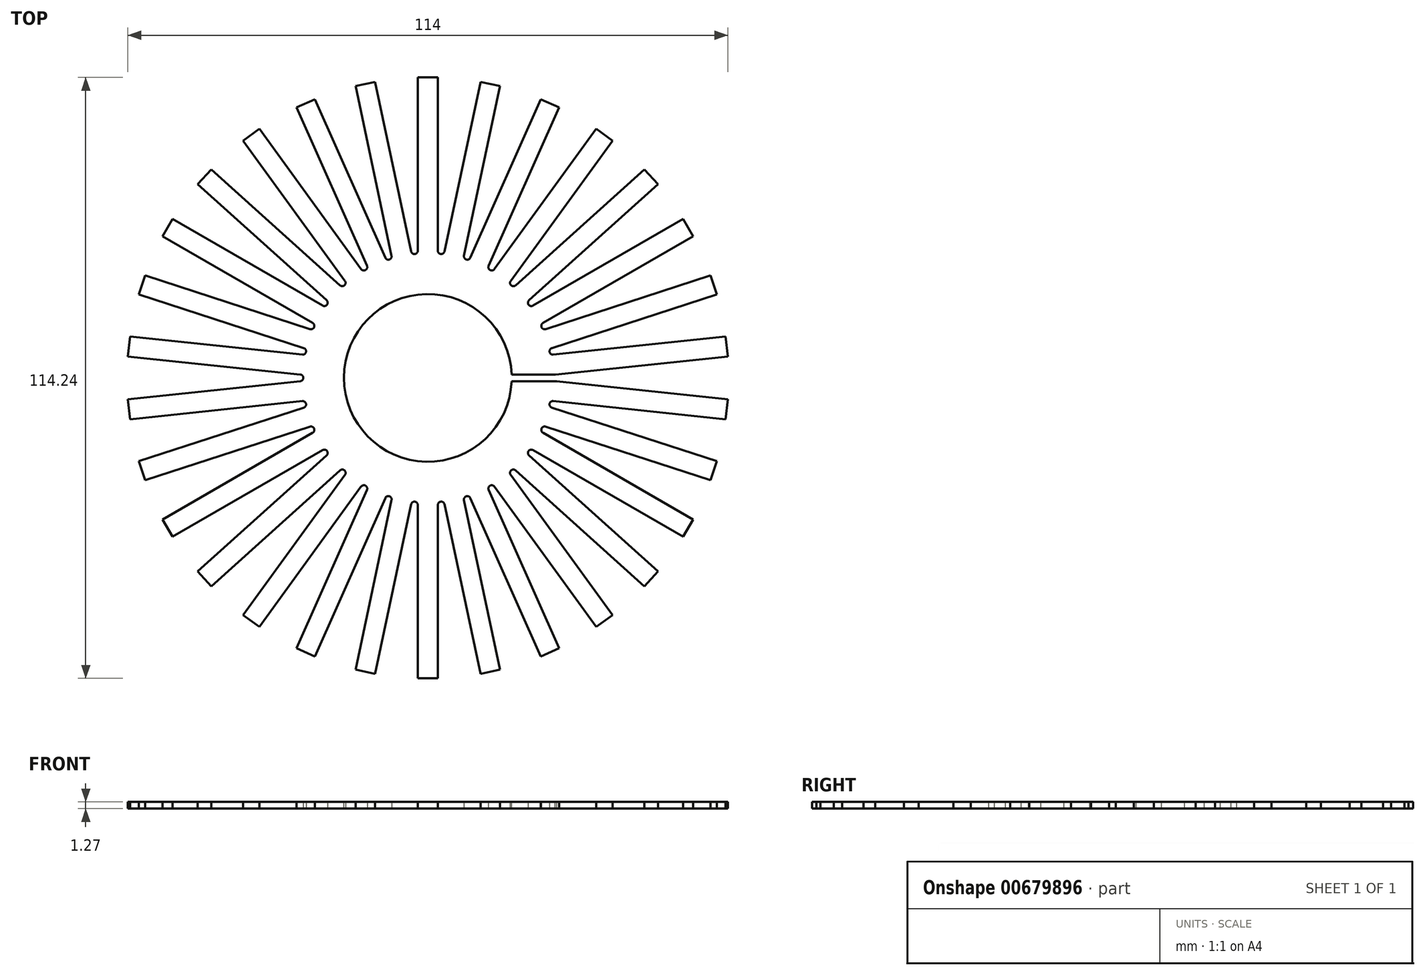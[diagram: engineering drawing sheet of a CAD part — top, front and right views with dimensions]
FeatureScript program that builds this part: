
annotation { "Feature Type Name" : "Feature", "Feature Type Description" : "" }
export const myFeature = defineFeature(function(context is Context, id is Id, definition is map)
    precondition{}
    {
        {
            var Q0;
            Q0=qCreatedBy(makeId("Top.planeOp"),FACE);
            var sketch = newSketch(context, id + "F0", { "sketchPlane" : qUnion([Q0])});
            skCircle(sketch, "E0", {"center": v(0, 0) * mm, "radius": 57.15 * mm, "construction": true});
            skCircle(sketch, "E1", {"center": v(0, 0) * mm, "radius": 13.34 * mm, "construction": true});
            skLineSegment(sketch, "E2.bottom", {"start": v(1.9, 13.2) * mm, "end": v(-1.9, 13.2) * mm});
            skLineSegment(sketch, "E2.top", {"start": v(1.9, 57.12) * mm, "end": v(-1.9, 57.12) * mm});
            skLineSegment(sketch, "E2.left", {"start": v(1.9, 13.2) * mm, "end": v(1.9, 57.12) * mm});
            skLineSegment(sketch, "E2.right", {"start": v(-1.9, 13.2) * mm, "end": v(-1.9, 57.12) * mm});
            skCircle(sketch, "E3.1.1", {"center": v(0, 0) * mm, "radius": 13.33 * mm, "construction": true});
            skLineSegment(sketch, "E3.1.2", {"start": v(-0.88, 13.3) * mm, "end": v(-10.01, 56.27) * mm});
            skLineSegment(sketch, "E3.1.3", {"start": v(-4.6, 12.51) * mm, "end": v(-13.74, 55.47) * mm});
            skLineSegment(sketch, "E3.1.4", {"start": v(-0.88, 13.3) * mm, "end": v(-4.6, 12.51) * mm});
            skLineSegment(sketch, "E3.1.5", {"start": v(-10.01, 56.27) * mm, "end": v(-13.74, 55.47) * mm});
            skLineSegment(sketch, "E3.2.2", {"start": v(-3.63, 12.83) * mm, "end": v(-21.5, 52.95) * mm});
            skLineSegment(sketch, "E3.2.3", {"start": v(-7.1, 11.28) * mm, "end": v(-24.97, 51.4) * mm});
            skLineSegment(sketch, "E3.2.4", {"start": v(-3.63, 12.83) * mm, "end": v(-7.1, 11.28) * mm});
            skLineSegment(sketch, "E3.2.5", {"start": v(-21.5, 52.95) * mm, "end": v(-24.97, 51.4) * mm});
            skLineSegment(sketch, "E3.3.2", {"start": v(-6.22, 11.8) * mm, "end": v(-32.03, 47.33) * mm});
            skLineSegment(sketch, "E3.3.3", {"start": v(-9.3, 9.56) * mm, "end": v(-35.11, 45.09) * mm});
            skLineSegment(sketch, "E3.3.4", {"start": v(-6.22, 11.8) * mm, "end": v(-9.3, 9.56) * mm});
            skLineSegment(sketch, "E3.3.5", {"start": v(-32.03, 47.33) * mm, "end": v(-35.11, 45.09) * mm});
            skCircle(sketch, "E3.4.1", {"center": v(0, 0) * mm, "radius": 13.33 * mm, "construction": true});
            skLineSegment(sketch, "E3.4.2", {"start": v(-8.53, 10.25) * mm, "end": v(-41.17, 39.64) * mm});
            skLineSegment(sketch, "E3.4.3", {"start": v(-11.08, 7.42) * mm, "end": v(-43.72, 36.8) * mm});
            skLineSegment(sketch, "E3.4.4", {"start": v(-8.53, 10.25) * mm, "end": v(-11.08, 7.42) * mm});
            skLineSegment(sketch, "E3.4.5", {"start": v(-41.17, 39.64) * mm, "end": v(-43.72, 36.8) * mm});
            skLineSegment(sketch, "E3.5.2", {"start": v(-10.48, 8.25) * mm, "end": v(-48.51, 30.2) * mm});
            skLineSegment(sketch, "E3.5.3", {"start": v(-12.38, 4.95) * mm, "end": v(-50.42, 26.9) * mm});
            skLineSegment(sketch, "E3.5.4", {"start": v(-10.48, 8.25) * mm, "end": v(-12.38, 4.95) * mm});
            skLineSegment(sketch, "E3.5.5", {"start": v(-48.51, 30.2) * mm, "end": v(-50.42, 26.9) * mm});
            skLineSegment(sketch, "E3.6.2", {"start": v(-11.96, 5.9) * mm, "end": v(-53.73, 19.46) * mm});
            skLineSegment(sketch, "E3.6.3", {"start": v(-13.14, 2.27) * mm, "end": v(-54.91, 15.84) * mm});
            skLineSegment(sketch, "E3.6.4", {"start": v(-11.96, 5.9) * mm, "end": v(-13.14, 2.27) * mm});
            skLineSegment(sketch, "E3.6.5", {"start": v(-53.73, 19.46) * mm, "end": v(-54.91, 15.84) * mm});
            skCircle(sketch, "E3.7.1", {"center": v(0, 0) * mm, "radius": 13.33 * mm, "construction": true});
            skLineSegment(sketch, "E3.7.2", {"start": v(-12.93, 3.27) * mm, "end": v(-56.6, 7.87) * mm});
            skLineSegment(sketch, "E3.7.3", {"start": v(-13.33, -0.51) * mm, "end": v(-57, 4.08) * mm});
            skLineSegment(sketch, "E3.7.4", {"start": v(-12.93, 3.27) * mm, "end": v(-13.33, -0.51) * mm});
            skLineSegment(sketch, "E3.7.5", {"start": v(-56.6, 7.87) * mm, "end": v(-57, 4.08) * mm});
            skLineSegment(sketch, "E3.8.2", {"start": v(-13.33, 0.51) * mm, "end": v(-57, -4.08) * mm});
            skLineSegment(sketch, "E3.8.3", {"start": v(-12.93, -3.27) * mm, "end": v(-56.6, -7.87) * mm});
            skLineSegment(sketch, "E3.8.4", {"start": v(-13.33, 0.51) * mm, "end": v(-12.93, -3.27) * mm});
            skLineSegment(sketch, "E3.8.5", {"start": v(-57, -4.08) * mm, "end": v(-56.6, -7.87) * mm});
            skLineSegment(sketch, "E3.9.2", {"start": v(-13.14, -2.27) * mm, "end": v(-54.91, -15.84) * mm});
            skLineSegment(sketch, "E3.9.3", {"start": v(-11.96, -5.9) * mm, "end": v(-53.73, -19.46) * mm});
            skLineSegment(sketch, "E3.9.4", {"start": v(-13.14, -2.27) * mm, "end": v(-11.96, -5.9) * mm});
            skLineSegment(sketch, "E3.9.5", {"start": v(-54.91, -15.84) * mm, "end": v(-53.73, -19.46) * mm});
            skLineSegment(sketch, "E3.10.2", {"start": v(-12.38, -4.95) * mm, "end": v(-50.42, -26.9) * mm});
            skLineSegment(sketch, "E3.10.3", {"start": v(-10.48, -8.25) * mm, "end": v(-48.51, -30.2) * mm});
            skLineSegment(sketch, "E3.10.4", {"start": v(-12.38, -4.95) * mm, "end": v(-10.48, -8.25) * mm});
            skLineSegment(sketch, "E3.10.5", {"start": v(-50.42, -26.9) * mm, "end": v(-48.51, -30.2) * mm});
            skLineSegment(sketch, "E3.11.2", {"start": v(-11.08, -7.42) * mm, "end": v(-43.72, -36.8) * mm});
            skLineSegment(sketch, "E3.11.3", {"start": v(-8.53, -10.25) * mm, "end": v(-41.17, -39.64) * mm});
            skLineSegment(sketch, "E3.11.4", {"start": v(-11.08, -7.42) * mm, "end": v(-8.53, -10.25) * mm});
            skLineSegment(sketch, "E3.11.5", {"start": v(-43.72, -36.8) * mm, "end": v(-41.17, -39.64) * mm});
            skLineSegment(sketch, "E3.12.2", {"start": v(-9.3, -9.56) * mm, "end": v(-35.11, -45.09) * mm});
            skLineSegment(sketch, "E3.12.3", {"start": v(-6.22, -11.8) * mm, "end": v(-32.03, -47.33) * mm});
            skLineSegment(sketch, "E3.12.4", {"start": v(-9.3, -9.56) * mm, "end": v(-6.22, -11.8) * mm});
            skLineSegment(sketch, "E3.12.5", {"start": v(-35.11, -45.09) * mm, "end": v(-32.03, -47.33) * mm});
            skLineSegment(sketch, "E3.13.2", {"start": v(-7.1, -11.28) * mm, "end": v(-24.97, -51.4) * mm});
            skLineSegment(sketch, "E3.13.3", {"start": v(-3.63, -12.83) * mm, "end": v(-21.5, -52.95) * mm});
            skLineSegment(sketch, "E3.13.4", {"start": v(-7.1, -11.28) * mm, "end": v(-3.63, -12.83) * mm});
            skLineSegment(sketch, "E3.13.5", {"start": v(-24.97, -51.4) * mm, "end": v(-21.5, -52.95) * mm});
            skCircle(sketch, "E3.14.1", {"center": v(0, 0) * mm, "radius": 13.33 * mm, "construction": true});
            skLineSegment(sketch, "E3.14.2", {"start": v(-4.6, -12.51) * mm, "end": v(-13.74, -55.47) * mm});
            skLineSegment(sketch, "E3.14.3", {"start": v(-0.88, -13.3) * mm, "end": v(-10.01, -56.27) * mm});
            skLineSegment(sketch, "E3.14.4", {"start": v(-4.6, -12.51) * mm, "end": v(-0.88, -13.3) * mm});
            skLineSegment(sketch, "E3.14.5", {"start": v(-13.74, -55.47) * mm, "end": v(-10.01, -56.27) * mm});
            skLineSegment(sketch, "E3.15.2", {"start": v(-1.9, -13.2) * mm, "end": v(-1.9, -57.12) * mm});
            skLineSegment(sketch, "E3.15.3", {"start": v(1.9, -13.2) * mm, "end": v(1.9, -57.12) * mm});
            skLineSegment(sketch, "E3.15.4", {"start": v(-1.9, -13.2) * mm, "end": v(1.9, -13.2) * mm});
            skLineSegment(sketch, "E3.15.5", {"start": v(-1.9, -57.12) * mm, "end": v(1.9, -57.12) * mm});
            skCircle(sketch, "E3.16.1", {"center": v(0, 0) * mm, "radius": 13.33 * mm, "construction": true});
            skLineSegment(sketch, "E3.16.2", {"start": v(0.88, -13.3) * mm, "end": v(10.01, -56.27) * mm});
            skLineSegment(sketch, "E3.16.3", {"start": v(4.6, -12.51) * mm, "end": v(13.74, -55.47) * mm});
            skLineSegment(sketch, "E3.16.4", {"start": v(0.88, -13.3) * mm, "end": v(4.6, -12.51) * mm});
            skLineSegment(sketch, "E3.16.5", {"start": v(10.01, -56.27) * mm, "end": v(13.74, -55.47) * mm});
            skLineSegment(sketch, "E3.17.2", {"start": v(3.63, -12.83) * mm, "end": v(21.5, -52.95) * mm});
            skLineSegment(sketch, "E3.17.3", {"start": v(7.1, -11.28) * mm, "end": v(24.97, -51.4) * mm});
            skLineSegment(sketch, "E3.17.4", {"start": v(3.63, -12.83) * mm, "end": v(7.1, -11.28) * mm});
            skLineSegment(sketch, "E3.17.5", {"start": v(21.5, -52.95) * mm, "end": v(24.97, -51.4) * mm});
            skLineSegment(sketch, "E3.18.2", {"start": v(6.22, -11.8) * mm, "end": v(32.03, -47.33) * mm});
            skLineSegment(sketch, "E3.18.3", {"start": v(9.3, -9.56) * mm, "end": v(35.11, -45.09) * mm});
            skLineSegment(sketch, "E3.18.4", {"start": v(6.22, -11.8) * mm, "end": v(9.3, -9.56) * mm});
            skLineSegment(sketch, "E3.18.5", {"start": v(32.03, -47.33) * mm, "end": v(35.11, -45.09) * mm});
            skCircle(sketch, "E3.19.1", {"center": v(0, 0) * mm, "radius": 13.33 * mm, "construction": true});
            skLineSegment(sketch, "E3.19.2", {"start": v(8.53, -10.25) * mm, "end": v(41.17, -39.64) * mm});
            skLineSegment(sketch, "E3.19.3", {"start": v(11.08, -7.42) * mm, "end": v(43.72, -36.8) * mm});
            skLineSegment(sketch, "E3.19.4", {"start": v(8.53, -10.25) * mm, "end": v(11.08, -7.42) * mm});
            skLineSegment(sketch, "E3.19.5", {"start": v(41.17, -39.64) * mm, "end": v(43.72, -36.8) * mm});
            skLineSegment(sketch, "E4.4.20.0", {"start": v(10.48, -8.25) * mm, "end": v(48.51, -30.2) * mm});
            skLineSegment(sketch, "E4.7.20.0", {"start": v(12.38, -4.95) * mm, "end": v(50.42, -26.9) * mm});
            skLineSegment(sketch, "E4.10.20.0", {"start": v(10.48, -8.25) * mm, "end": v(12.38, -4.95) * mm});
            skLineSegment(sketch, "E4.13.20.0", {"start": v(48.51, -30.2) * mm, "end": v(50.42, -26.9) * mm});
            skLineSegment(sketch, "E4.4.21.0", {"start": v(11.96, -5.9) * mm, "end": v(53.73, -19.46) * mm});
            skLineSegment(sketch, "E4.7.21.0", {"start": v(13.14, -2.27) * mm, "end": v(54.91, -15.84) * mm});
            skLineSegment(sketch, "E4.10.21.0", {"start": v(11.96, -5.9) * mm, "end": v(13.14, -2.27) * mm});
            skLineSegment(sketch, "E4.13.21.0", {"start": v(53.73, -19.46) * mm, "end": v(54.91, -15.84) * mm});
            skLineSegment(sketch, "E4.4.22.0", {"start": v(12.93, -3.27) * mm, "end": v(56.6, -7.87) * mm});
            skLineSegment(sketch, "E4.7.22.0", {"start": v(13.33, 0.51) * mm, "end": v(57, -4.08) * mm});
            skLineSegment(sketch, "E4.10.22.0", {"start": v(12.93, -3.27) * mm, "end": v(13.33, 0.51) * mm});
            skLineSegment(sketch, "E4.13.22.0", {"start": v(56.6, -7.87) * mm, "end": v(57, -4.08) * mm});
            skLineSegment(sketch, "E4.4.23.0", {"start": v(13.33, -0.51) * mm, "end": v(57, 4.08) * mm});
            skLineSegment(sketch, "E4.7.23.0", {"start": v(12.93, 3.27) * mm, "end": v(56.6, 7.87) * mm});
            skLineSegment(sketch, "E4.10.23.0", {"start": v(13.33, -0.51) * mm, "end": v(12.93, 3.27) * mm});
            skLineSegment(sketch, "E4.13.23.0", {"start": v(57, 4.08) * mm, "end": v(56.6, 7.87) * mm});
            skLineSegment(sketch, "E4.4.24.0", {"start": v(13.14, 2.27) * mm, "end": v(54.91, 15.84) * mm});
            skLineSegment(sketch, "E4.7.24.0", {"start": v(11.96, 5.9) * mm, "end": v(53.73, 19.46) * mm});
            skLineSegment(sketch, "E4.10.24.0", {"start": v(13.14, 2.27) * mm, "end": v(11.96, 5.9) * mm});
            skLineSegment(sketch, "E4.13.24.0", {"start": v(54.91, 15.84) * mm, "end": v(53.73, 19.46) * mm});
            skLineSegment(sketch, "E5.4.25.0", {"start": v(12.38, 4.95) * mm, "end": v(50.42, 26.9) * mm});
            skLineSegment(sketch, "E5.7.25.0", {"start": v(10.48, 8.25) * mm, "end": v(48.51, 30.2) * mm});
            skLineSegment(sketch, "E5.10.25.0", {"start": v(12.38, 4.95) * mm, "end": v(10.48, 8.25) * mm});
            skLineSegment(sketch, "E5.13.25.0", {"start": v(50.42, 26.9) * mm, "end": v(48.51, 30.2) * mm});
            skLineSegment(sketch, "E5.4.26.0", {"start": v(11.08, 7.42) * mm, "end": v(43.72, 36.8) * mm});
            skLineSegment(sketch, "E5.7.26.0", {"start": v(8.53, 10.25) * mm, "end": v(41.17, 39.64) * mm});
            skLineSegment(sketch, "E5.10.26.0", {"start": v(11.08, 7.42) * mm, "end": v(8.53, 10.25) * mm});
            skLineSegment(sketch, "E5.13.26.0", {"start": v(43.72, 36.8) * mm, "end": v(41.17, 39.64) * mm});
            skLineSegment(sketch, "E5.4.27.0", {"start": v(9.3, 9.56) * mm, "end": v(35.11, 45.09) * mm});
            skLineSegment(sketch, "E5.7.27.0", {"start": v(6.22, 11.8) * mm, "end": v(32.03, 47.33) * mm});
            skLineSegment(sketch, "E5.10.27.0", {"start": v(9.3, 9.56) * mm, "end": v(6.22, 11.8) * mm});
            skLineSegment(sketch, "E5.13.27.0", {"start": v(35.11, 45.09) * mm, "end": v(32.03, 47.33) * mm});
            skLineSegment(sketch, "E5.4.28.0", {"start": v(7.1, 11.28) * mm, "end": v(24.97, 51.4) * mm});
            skLineSegment(sketch, "E5.7.28.0", {"start": v(3.63, 12.83) * mm, "end": v(21.5, 52.95) * mm});
            skLineSegment(sketch, "E5.10.28.0", {"start": v(7.1, 11.28) * mm, "end": v(3.63, 12.83) * mm});
            skLineSegment(sketch, "E5.13.28.0", {"start": v(24.97, 51.4) * mm, "end": v(21.5, 52.95) * mm});
            skLineSegment(sketch, "E5.4.29.0", {"start": v(4.6, 12.51) * mm, "end": v(13.74, 55.47) * mm});
            skLineSegment(sketch, "E5.7.29.0", {"start": v(0.88, 13.3) * mm, "end": v(10.01, 56.27) * mm});
            skLineSegment(sketch, "E5.10.29.0", {"start": v(4.6, 12.51) * mm, "end": v(0.88, 13.3) * mm});
            skLineSegment(sketch, "E5.13.29.0", {"start": v(13.74, 55.47) * mm, "end": v(10.01, 56.27) * mm});
            skSolve(sketch);
        }
        {
            var Q0;
            Q0 = qSketchRegion(id + "F0", true);
            extrude(context, id + "F1", {"entities" : qUnion([Q0]), "depth" : 1.27 * mm, "offsetDistance" : 25.4 * mm});
        }
        {
            var Q0;
            Q0=makeQuery(id+"F1.opExtrude","CAP_FACE",FACE,{"disambiguationData":[OSD([sQuery(id+"F0.wireOp",EDGE,"E2.bottom"),sQuery(id+"F0.wireOp",EDGE,"E2.top"),sQuery(id+"F0.wireOp",EDGE,"E2.left"),sQuery(id+"F0.wireOp",EDGE,"E2.right"),sQuery(id+"F0.wireOp",EDGE,"E3.1.2"),sQuery(id+"F0.wireOp",EDGE,"E3.1.3"),sQuery(id+"F0.wireOp",EDGE,"E3.1.4"),sQuery(id+"F0.wireOp",EDGE,"E3.1.5"),sQuery(id+"F0.wireOp",EDGE,"E3.2.2"),sQuery(id+"F0.wireOp",EDGE,"E3.2.3"),sQuery(id+"F0.wireOp",EDGE,"E3.2.4"),sQuery(id+"F0.wireOp",EDGE,"E3.2.5"),sQuery(id+"F0.wireOp",EDGE,"E3.3.2"),sQuery(id+"F0.wireOp",EDGE,"E3.3.3"),sQuery(id+"F0.wireOp",EDGE,"E3.3.4"),sQuery(id+"F0.wireOp",EDGE,"E3.3.5"),sQuery(id+"F0.wireOp",EDGE,"E3.4.2"),sQuery(id+"F0.wireOp",EDGE,"E3.4.3"),sQuery(id+"F0.wireOp",EDGE,"E3.4.4"),sQuery(id+"F0.wireOp",EDGE,"E3.4.5"),sQuery(id+"F0.wireOp",EDGE,"E3.5.2"),sQuery(id+"F0.wireOp",EDGE,"E3.5.3"),sQuery(id+"F0.wireOp",EDGE,"E3.5.4"),sQuery(id+"F0.wireOp",EDGE,"E3.5.5"),sQuery(id+"F0.wireOp",EDGE,"E3.6.2"),sQuery(id+"F0.wireOp",EDGE,"E3.6.3"),sQuery(id+"F0.wireOp",EDGE,"E3.6.4"),sQuery(id+"F0.wireOp",EDGE,"E3.6.5"),sQuery(id+"F0.wireOp",EDGE,"E3.7.2"),sQuery(id+"F0.wireOp",EDGE,"E3.7.3"),sQuery(id+"F0.wireOp",EDGE,"E3.7.4"),sQuery(id+"F0.wireOp",EDGE,"E3.7.5"),sQuery(id+"F0.wireOp",EDGE,"E3.8.2"),sQuery(id+"F0.wireOp",EDGE,"E3.8.3"),sQuery(id+"F0.wireOp",EDGE,"E3.8.4"),sQuery(id+"F0.wireOp",EDGE,"E3.8.5"),sQuery(id+"F0.wireOp",EDGE,"E3.9.2"),sQuery(id+"F0.wireOp",EDGE,"E3.9.3"),sQuery(id+"F0.wireOp",EDGE,"E3.9.4"),sQuery(id+"F0.wireOp",EDGE,"E3.9.5"),sQuery(id+"F0.wireOp",EDGE,"E3.10.2"),sQuery(id+"F0.wireOp",EDGE,"E3.10.3"),sQuery(id+"F0.wireOp",EDGE,"E3.10.4"),sQuery(id+"F0.wireOp",EDGE,"E3.10.5"),sQuery(id+"F0.wireOp",EDGE,"E3.11.2"),sQuery(id+"F0.wireOp",EDGE,"E3.11.3"),sQuery(id+"F0.wireOp",EDGE,"E3.11.4"),sQuery(id+"F0.wireOp",EDGE,"E3.11.5"),sQuery(id+"F0.wireOp",EDGE,"E3.12.2"),sQuery(id+"F0.wireOp",EDGE,"E3.12.3"),sQuery(id+"F0.wireOp",EDGE,"E3.12.4"),sQuery(id+"F0.wireOp",EDGE,"E3.12.5"),sQuery(id+"F0.wireOp",EDGE,"E3.13.2"),sQuery(id+"F0.wireOp",EDGE,"E3.13.3"),sQuery(id+"F0.wireOp",EDGE,"E3.13.4"),sQuery(id+"F0.wireOp",EDGE,"E3.13.5"),sQuery(id+"F0.wireOp",EDGE,"E3.14.2"),sQuery(id+"F0.wireOp",EDGE,"E3.14.3"),sQuery(id+"F0.wireOp",EDGE,"E3.14.4"),sQuery(id+"F0.wireOp",EDGE,"E3.14.5"),sQuery(id+"F0.wireOp",EDGE,"E3.15.2"),sQuery(id+"F0.wireOp",EDGE,"E3.15.3"),sQuery(id+"F0.wireOp",EDGE,"E3.15.4"),sQuery(id+"F0.wireOp",EDGE,"E3.15.5"),sQuery(id+"F0.wireOp",EDGE,"E3.16.2"),sQuery(id+"F0.wireOp",EDGE,"E3.16.3"),sQuery(id+"F0.wireOp",EDGE,"E3.16.4"),sQuery(id+"F0.wireOp",EDGE,"E3.16.5"),sQuery(id+"F0.wireOp",EDGE,"E3.17.2"),sQuery(id+"F0.wireOp",EDGE,"E3.17.3"),sQuery(id+"F0.wireOp",EDGE,"E3.17.4"),sQuery(id+"F0.wireOp",EDGE,"E3.17.5"),sQuery(id+"F0.wireOp",EDGE,"E3.18.2"),sQuery(id+"F0.wireOp",EDGE,"E3.18.3"),sQuery(id+"F0.wireOp",EDGE,"E3.18.4"),sQuery(id+"F0.wireOp",EDGE,"E3.18.5"),sQuery(id+"F0.wireOp",EDGE,"E3.19.2"),sQuery(id+"F0.wireOp",EDGE,"E3.19.3"),sQuery(id+"F0.wireOp",EDGE,"E3.19.4"),sQuery(id+"F0.wireOp",EDGE,"E3.19.5"),sQuery(id+"F0.wireOp",EDGE,"E4.4.20.0"),sQuery(id+"F0.wireOp",EDGE,"E4.7.20.0"),sQuery(id+"F0.wireOp",EDGE,"E4.10.20.0"),sQuery(id+"F0.wireOp",EDGE,"E4.13.20.0"),sQuery(id+"F0.wireOp",EDGE,"E4.4.21.0"),sQuery(id+"F0.wireOp",EDGE,"E4.7.21.0"),sQuery(id+"F0.wireOp",EDGE,"E4.10.21.0"),sQuery(id+"F0.wireOp",EDGE,"E4.13.21.0"),sQuery(id+"F0.wireOp",EDGE,"E4.4.22.0"),sQuery(id+"F0.wireOp",EDGE,"E4.7.22.0"),sQuery(id+"F0.wireOp",EDGE,"E4.10.22.0"),sQuery(id+"F0.wireOp",EDGE,"E4.13.22.0"),sQuery(id+"F0.wireOp",EDGE,"E4.4.23.0"),sQuery(id+"F0.wireOp",EDGE,"E4.7.23.0"),sQuery(id+"F0.wireOp",EDGE,"E4.10.23.0"),sQuery(id+"F0.wireOp",EDGE,"E4.13.23.0"),sQuery(id+"F0.wireOp",EDGE,"E4.4.24.0"),sQuery(id+"F0.wireOp",EDGE,"E4.7.24.0"),sQuery(id+"F0.wireOp",EDGE,"E4.10.24.0"),sQuery(id+"F0.wireOp",EDGE,"E4.13.24.0"),sQuery(id+"F0.wireOp",EDGE,"E5.4.25.0"),sQuery(id+"F0.wireOp",EDGE,"E5.7.25.0"),sQuery(id+"F0.wireOp",EDGE,"E5.10.25.0"),sQuery(id+"F0.wireOp",EDGE,"E5.13.25.0"),sQuery(id+"F0.wireOp",EDGE,"E5.4.26.0"),sQuery(id+"F0.wireOp",EDGE,"E5.7.26.0"),sQuery(id+"F0.wireOp",EDGE,"E5.10.26.0"),sQuery(id+"F0.wireOp",EDGE,"E5.13.26.0"),sQuery(id+"F0.wireOp",EDGE,"E5.4.27.0"),sQuery(id+"F0.wireOp",EDGE,"E5.7.27.0"),sQuery(id+"F0.wireOp",EDGE,"E5.10.27.0"),sQuery(id+"F0.wireOp",EDGE,"E5.13.27.0"),sQuery(id+"F0.wireOp",EDGE,"E5.4.28.0"),sQuery(id+"F0.wireOp",EDGE,"E5.7.28.0"),sQuery(id+"F0.wireOp",EDGE,"E5.10.28.0"),sQuery(id+"F0.wireOp",EDGE,"E5.13.28.0"),sQuery(id+"F0.wireOp",EDGE,"E5.4.29.0"),sQuery(id+"F0.wireOp",EDGE,"E5.7.29.0"),sQuery(id+"F0.wireOp",EDGE,"E5.10.29.0"),sQuery(id+"F0.wireOp",EDGE,"E5.13.29.0")])],"isStart":false});
            var sketch = newSketch(context, id + "F2", { "sketchPlane" : qUnion([Q0])});
            skCircle(sketch, "E6", {"center": v(0, 0) * mm, "radius": 15.94 * mm});
            skSolve(sketch);
        }
        {
            var Q0;
            Q0 = qSketchRegion(id + "F2", true);
            extrude(context, id + "F3", {"entities" : qUnion([Q0]), "operationType" : NewBodyOperationType.REMOVE, "oppositeDirection" : true, "depth" : 25.4 * mm, "offsetDistance" : 25.4 * mm});
        }
        {
            var Q0;
            Q0=makeQuery(id+"F1.opExtrude","SWEPT_EDGE",EDGE,{"disambiguationData":[OSD([sQuery(id+"F0.wireOp",EDGE,"E3.3.3"),sQuery(id+"F0.wireOp",EDGE,"E3.4.2")])]});
            fillet(context, id + "F4", {"entities" : qUnion([Q0]), "radius" : 0.64 * mm, "tangentPropagation" : true, "allowEdgeOverflow" : false});
        }
        {
            var Q0;
            Q0=makeQuery(id+"F1.opExtrude","SWEPT_EDGE",EDGE,{"disambiguationData":[OSD([sQuery(id+"F0.wireOp",EDGE,"E3.2.3"),sQuery(id+"F0.wireOp",EDGE,"E3.3.2")])]});
            var Q1;
            Q1=makeQuery(id+"F1.opExtrude","SWEPT_EDGE",EDGE,{"disambiguationData":[OSD([sQuery(id+"F0.wireOp",EDGE,"E2.right"),sQuery(id+"F0.wireOp",EDGE,"E3.1.2")])]});
            var Q2;
            Q2=makeQuery(id+"F1.opExtrude","SWEPT_EDGE",EDGE,{"disambiguationData":[OSD([sQuery(id+"F0.wireOp",EDGE,"E2.left"),sQuery(id+"F0.wireOp",EDGE,"E5.7.29.0")])]});
            var Q3;
            Q3=makeQuery(id+"F1.opExtrude","SWEPT_EDGE",EDGE,{"disambiguationData":[OSD([sQuery(id+"F0.wireOp",EDGE,"E5.7.28.0"),sQuery(id+"F0.wireOp",EDGE,"E5.4.29.0")])]});
            var Q4;
            Q4=makeQuery(id+"F1.opExtrude","SWEPT_EDGE",EDGE,{"disambiguationData":[OSD([sQuery(id+"F0.wireOp",EDGE,"E5.7.27.0"),sQuery(id+"F0.wireOp",EDGE,"E5.4.28.0")])]});
            var Q5;
            Q5=makeQuery(id+"F1.opExtrude","SWEPT_EDGE",EDGE,{"disambiguationData":[OSD([sQuery(id+"F0.wireOp",EDGE,"E5.7.26.0"),sQuery(id+"F0.wireOp",EDGE,"E5.4.27.0")])]});
            var Q6;
            Q6=makeQuery(id+"F1.opExtrude","SWEPT_EDGE",EDGE,{"disambiguationData":[OSD([sQuery(id+"F0.wireOp",EDGE,"E5.7.25.0"),sQuery(id+"F0.wireOp",EDGE,"E5.4.26.0")])]});
            var Q7;
            Q7=makeQuery(id+"F1.opExtrude","SWEPT_EDGE",EDGE,{"disambiguationData":[OSD([sQuery(id+"F0.wireOp",EDGE,"E4.7.24.0"),sQuery(id+"F0.wireOp",EDGE,"E5.4.25.0")])]});
            var Q8;
            Q8=makeQuery(id+"F1.opExtrude","SWEPT_EDGE",EDGE,{"disambiguationData":[OSD([sQuery(id+"F0.wireOp",EDGE,"E4.7.23.0"),sQuery(id+"F0.wireOp",EDGE,"E4.4.24.0")])]});
            var Q9;
            Q9=makeQuery(id+"F1.opExtrude","SWEPT_EDGE",EDGE,{"disambiguationData":[OSD([sQuery(id+"F0.wireOp",EDGE,"E4.7.22.0"),sQuery(id+"F0.wireOp",EDGE,"E4.4.23.0")])]});
            var Q10;
            Q10=makeQuery(id+"F1.opExtrude","SWEPT_EDGE",EDGE,{"disambiguationData":[OSD([sQuery(id+"F0.wireOp",EDGE,"E4.7.21.0"),sQuery(id+"F0.wireOp",EDGE,"E4.4.22.0")])]});
            var Q11;
            Q11=makeQuery(id+"F1.opExtrude","SWEPT_EDGE",EDGE,{"disambiguationData":[OSD([sQuery(id+"F0.wireOp",EDGE,"E4.7.20.0"),sQuery(id+"F0.wireOp",EDGE,"E4.4.21.0")])]});
            var Q12;
            Q12=makeQuery(id+"F1.opExtrude","SWEPT_EDGE",EDGE,{"disambiguationData":[OSD([sQuery(id+"F0.wireOp",EDGE,"E3.19.3"),sQuery(id+"F0.wireOp",EDGE,"E4.4.20.0")])]});
            var Q13;
            Q13=makeQuery(id+"F1.opExtrude","SWEPT_EDGE",EDGE,{"disambiguationData":[OSD([sQuery(id+"F0.wireOp",EDGE,"E3.18.3"),sQuery(id+"F0.wireOp",EDGE,"E3.19.2")])]});
            var Q14;
            Q14=makeQuery(id+"F1.opExtrude","SWEPT_EDGE",EDGE,{"disambiguationData":[OSD([sQuery(id+"F0.wireOp",EDGE,"E3.17.3"),sQuery(id+"F0.wireOp",EDGE,"E3.18.2")])]});
            var Q15;
            Q15=makeQuery(id+"F1.opExtrude","SWEPT_EDGE",EDGE,{"disambiguationData":[OSD([sQuery(id+"F0.wireOp",EDGE,"E3.16.3"),sQuery(id+"F0.wireOp",EDGE,"E3.17.2")])]});
            var Q16;
            Q16=makeQuery(id+"F1.opExtrude","SWEPT_EDGE",EDGE,{"disambiguationData":[OSD([sQuery(id+"F0.wireOp",EDGE,"E3.15.3"),sQuery(id+"F0.wireOp",EDGE,"E3.16.2")])]});
            var Q17;
            Q17=makeQuery(id+"F1.opExtrude","SWEPT_EDGE",EDGE,{"disambiguationData":[OSD([sQuery(id+"F0.wireOp",EDGE,"E3.14.3"),sQuery(id+"F0.wireOp",EDGE,"E3.15.2")])]});
            var Q18;
            Q18=makeQuery(id+"F1.opExtrude","SWEPT_EDGE",EDGE,{"disambiguationData":[OSD([sQuery(id+"F0.wireOp",EDGE,"E3.13.3"),sQuery(id+"F0.wireOp",EDGE,"E3.14.2")])]});
            var Q19;
            Q19=makeQuery(id+"F1.opExtrude","SWEPT_EDGE",EDGE,{"disambiguationData":[OSD([sQuery(id+"F0.wireOp",EDGE,"E3.12.3"),sQuery(id+"F0.wireOp",EDGE,"E3.13.2")])]});
            var Q20;
            Q20=makeQuery(id+"F1.opExtrude","SWEPT_EDGE",EDGE,{"disambiguationData":[OSD([sQuery(id+"F0.wireOp",EDGE,"E3.11.3"),sQuery(id+"F0.wireOp",EDGE,"E3.12.2")])]});
            var Q21;
            Q21=makeQuery(id+"F1.opExtrude","SWEPT_EDGE",EDGE,{"disambiguationData":[OSD([sQuery(id+"F0.wireOp",EDGE,"E3.10.3"),sQuery(id+"F0.wireOp",EDGE,"E3.11.2")])]});
            var Q22;
            Q22=makeQuery(id+"F1.opExtrude","SWEPT_EDGE",EDGE,{"disambiguationData":[OSD([sQuery(id+"F0.wireOp",EDGE,"E3.9.3"),sQuery(id+"F0.wireOp",EDGE,"E3.10.2")])]});
            var Q23;
            Q23=makeQuery(id+"F1.opExtrude","SWEPT_EDGE",EDGE,{"disambiguationData":[OSD([sQuery(id+"F0.wireOp",EDGE,"E3.8.3"),sQuery(id+"F0.wireOp",EDGE,"E3.9.2")])]});
            var Q24;
            Q24=makeQuery(id+"F1.opExtrude","SWEPT_EDGE",EDGE,{"disambiguationData":[OSD([sQuery(id+"F0.wireOp",EDGE,"E3.7.3"),sQuery(id+"F0.wireOp",EDGE,"E3.8.2")])]});
            var Q25;
            Q25=makeQuery(id+"F1.opExtrude","SWEPT_EDGE",EDGE,{"disambiguationData":[OSD([sQuery(id+"F0.wireOp",EDGE,"E3.6.3"),sQuery(id+"F0.wireOp",EDGE,"E3.7.2")])]});
            var Q26;
            Q26=makeQuery(id+"F1.opExtrude","SWEPT_EDGE",EDGE,{"disambiguationData":[OSD([sQuery(id+"F0.wireOp",EDGE,"E3.5.3"),sQuery(id+"F0.wireOp",EDGE,"E3.6.2")])]});
            var Q27;
            Q27=makeQuery(id+"F1.opExtrude","SWEPT_EDGE",EDGE,{"disambiguationData":[OSD([sQuery(id+"F0.wireOp",EDGE,"E3.4.3"),sQuery(id+"F0.wireOp",EDGE,"E3.5.2")])]});
            fillet(context, id + "F5", {"entities" : qUnion([Q0, Q1, Q2, Q3, Q4, Q5, Q6, Q7, Q8, Q9, Q10, Q11, Q12, Q13, Q14, Q15, Q16, Q17, Q18, Q19, Q20, Q21, Q22, Q23, Q24, Q25, Q26, Q27]), "radius" : 0.64 * mm, "tangentPropagation" : true, "allowEdgeOverflow" : false});
        }
        {
            var Q0;
            Q0=makeQuery(id+"F1.opExtrude","SWEPT_EDGE",EDGE,{"disambiguationData":[OSD([sQuery(id+"F0.wireOp",EDGE,"E3.1.3"),sQuery(id+"F0.wireOp",EDGE,"E3.2.2")])]});
            fillet(context, id + "F6", {"entities" : qUnion([Q0]), "radius" : 0.64 * mm, "tangentPropagation" : true, "allowEdgeOverflow" : false});
        }
        {
            var Q0;
            Q0=makeQuery(id+"F1.opExtrude","CAP_FACE",FACE,{"disambiguationData":[OSD([sQuery(id+"F0.wireOp",EDGE,"E2.bottom"),sQuery(id+"F0.wireOp",EDGE,"E2.top"),sQuery(id+"F0.wireOp",EDGE,"E2.left"),sQuery(id+"F0.wireOp",EDGE,"E2.right"),sQuery(id+"F0.wireOp",EDGE,"E3.1.2"),sQuery(id+"F0.wireOp",EDGE,"E3.1.3"),sQuery(id+"F0.wireOp",EDGE,"E3.1.4"),sQuery(id+"F0.wireOp",EDGE,"E3.1.5"),sQuery(id+"F0.wireOp",EDGE,"E3.2.2"),sQuery(id+"F0.wireOp",EDGE,"E3.2.3"),sQuery(id+"F0.wireOp",EDGE,"E3.2.4"),sQuery(id+"F0.wireOp",EDGE,"E3.2.5"),sQuery(id+"F0.wireOp",EDGE,"E3.3.2"),sQuery(id+"F0.wireOp",EDGE,"E3.3.3"),sQuery(id+"F0.wireOp",EDGE,"E3.3.4"),sQuery(id+"F0.wireOp",EDGE,"E3.3.5"),sQuery(id+"F0.wireOp",EDGE,"E3.4.2"),sQuery(id+"F0.wireOp",EDGE,"E3.4.3"),sQuery(id+"F0.wireOp",EDGE,"E3.4.4"),sQuery(id+"F0.wireOp",EDGE,"E3.4.5"),sQuery(id+"F0.wireOp",EDGE,"E3.5.2"),sQuery(id+"F0.wireOp",EDGE,"E3.5.3"),sQuery(id+"F0.wireOp",EDGE,"E3.5.4"),sQuery(id+"F0.wireOp",EDGE,"E3.5.5"),sQuery(id+"F0.wireOp",EDGE,"E3.6.2"),sQuery(id+"F0.wireOp",EDGE,"E3.6.3"),sQuery(id+"F0.wireOp",EDGE,"E3.6.4"),sQuery(id+"F0.wireOp",EDGE,"E3.6.5"),sQuery(id+"F0.wireOp",EDGE,"E3.7.2"),sQuery(id+"F0.wireOp",EDGE,"E3.7.3"),sQuery(id+"F0.wireOp",EDGE,"E3.7.4"),sQuery(id+"F0.wireOp",EDGE,"E3.7.5"),sQuery(id+"F0.wireOp",EDGE,"E3.8.2"),sQuery(id+"F0.wireOp",EDGE,"E3.8.3"),sQuery(id+"F0.wireOp",EDGE,"E3.8.4"),sQuery(id+"F0.wireOp",EDGE,"E3.8.5"),sQuery(id+"F0.wireOp",EDGE,"E3.9.2"),sQuery(id+"F0.wireOp",EDGE,"E3.9.3"),sQuery(id+"F0.wireOp",EDGE,"E3.9.4"),sQuery(id+"F0.wireOp",EDGE,"E3.9.5"),sQuery(id+"F0.wireOp",EDGE,"E3.10.2"),sQuery(id+"F0.wireOp",EDGE,"E3.10.3"),sQuery(id+"F0.wireOp",EDGE,"E3.10.4"),sQuery(id+"F0.wireOp",EDGE,"E3.10.5"),sQuery(id+"F0.wireOp",EDGE,"E3.11.2"),sQuery(id+"F0.wireOp",EDGE,"E3.11.3"),sQuery(id+"F0.wireOp",EDGE,"E3.11.4"),sQuery(id+"F0.wireOp",EDGE,"E3.11.5"),sQuery(id+"F0.wireOp",EDGE,"E3.12.2"),sQuery(id+"F0.wireOp",EDGE,"E3.12.3"),sQuery(id+"F0.wireOp",EDGE,"E3.12.4"),sQuery(id+"F0.wireOp",EDGE,"E3.12.5"),sQuery(id+"F0.wireOp",EDGE,"E3.13.2"),sQuery(id+"F0.wireOp",EDGE,"E3.13.3"),sQuery(id+"F0.wireOp",EDGE,"E3.13.4"),sQuery(id+"F0.wireOp",EDGE,"E3.13.5"),sQuery(id+"F0.wireOp",EDGE,"E3.14.2"),sQuery(id+"F0.wireOp",EDGE,"E3.14.3"),sQuery(id+"F0.wireOp",EDGE,"E3.14.4"),sQuery(id+"F0.wireOp",EDGE,"E3.14.5"),sQuery(id+"F0.wireOp",EDGE,"E3.15.2"),sQuery(id+"F0.wireOp",EDGE,"E3.15.3"),sQuery(id+"F0.wireOp",EDGE,"E3.15.4"),sQuery(id+"F0.wireOp",EDGE,"E3.15.5"),sQuery(id+"F0.wireOp",EDGE,"E3.16.2"),sQuery(id+"F0.wireOp",EDGE,"E3.16.3"),sQuery(id+"F0.wireOp",EDGE,"E3.16.4"),sQuery(id+"F0.wireOp",EDGE,"E3.16.5"),sQuery(id+"F0.wireOp",EDGE,"E3.17.2"),sQuery(id+"F0.wireOp",EDGE,"E3.17.3"),sQuery(id+"F0.wireOp",EDGE,"E3.17.4"),sQuery(id+"F0.wireOp",EDGE,"E3.17.5"),sQuery(id+"F0.wireOp",EDGE,"E3.18.2"),sQuery(id+"F0.wireOp",EDGE,"E3.18.3"),sQuery(id+"F0.wireOp",EDGE,"E3.18.4"),sQuery(id+"F0.wireOp",EDGE,"E3.18.5"),sQuery(id+"F0.wireOp",EDGE,"E3.19.2"),sQuery(id+"F0.wireOp",EDGE,"E3.19.3"),sQuery(id+"F0.wireOp",EDGE,"E3.19.4"),sQuery(id+"F0.wireOp",EDGE,"E3.19.5"),sQuery(id+"F0.wireOp",EDGE,"E4.4.20.0"),sQuery(id+"F0.wireOp",EDGE,"E4.7.20.0"),sQuery(id+"F0.wireOp",EDGE,"E4.10.20.0"),sQuery(id+"F0.wireOp",EDGE,"E4.13.20.0"),sQuery(id+"F0.wireOp",EDGE,"E4.4.21.0"),sQuery(id+"F0.wireOp",EDGE,"E4.7.21.0"),sQuery(id+"F0.wireOp",EDGE,"E4.10.21.0"),sQuery(id+"F0.wireOp",EDGE,"E4.13.21.0"),sQuery(id+"F0.wireOp",EDGE,"E4.4.22.0"),sQuery(id+"F0.wireOp",EDGE,"E4.7.22.0"),sQuery(id+"F0.wireOp",EDGE,"E4.10.22.0"),sQuery(id+"F0.wireOp",EDGE,"E4.13.22.0"),sQuery(id+"F0.wireOp",EDGE,"E4.4.23.0"),sQuery(id+"F0.wireOp",EDGE,"E4.7.23.0"),sQuery(id+"F0.wireOp",EDGE,"E4.10.23.0"),sQuery(id+"F0.wireOp",EDGE,"E4.13.23.0"),sQuery(id+"F0.wireOp",EDGE,"E4.4.24.0"),sQuery(id+"F0.wireOp",EDGE,"E4.7.24.0"),sQuery(id+"F0.wireOp",EDGE,"E4.10.24.0"),sQuery(id+"F0.wireOp",EDGE,"E4.13.24.0"),sQuery(id+"F0.wireOp",EDGE,"E5.4.25.0"),sQuery(id+"F0.wireOp",EDGE,"E5.7.25.0"),sQuery(id+"F0.wireOp",EDGE,"E5.10.25.0"),sQuery(id+"F0.wireOp",EDGE,"E5.13.25.0"),sQuery(id+"F0.wireOp",EDGE,"E5.4.26.0"),sQuery(id+"F0.wireOp",EDGE,"E5.7.26.0"),sQuery(id+"F0.wireOp",EDGE,"E5.10.26.0"),sQuery(id+"F0.wireOp",EDGE,"E5.13.26.0"),sQuery(id+"F0.wireOp",EDGE,"E5.4.27.0"),sQuery(id+"F0.wireOp",EDGE,"E5.7.27.0"),sQuery(id+"F0.wireOp",EDGE,"E5.10.27.0"),sQuery(id+"F0.wireOp",EDGE,"E5.13.27.0"),sQuery(id+"F0.wireOp",EDGE,"E5.4.28.0"),sQuery(id+"F0.wireOp",EDGE,"E5.7.28.0"),sQuery(id+"F0.wireOp",EDGE,"E5.10.28.0"),sQuery(id+"F0.wireOp",EDGE,"E5.13.28.0"),sQuery(id+"F0.wireOp",EDGE,"E5.4.29.0"),sQuery(id+"F0.wireOp",EDGE,"E5.7.29.0"),sQuery(id+"F0.wireOp",EDGE,"E5.10.29.0"),sQuery(id+"F0.wireOp",EDGE,"E5.13.29.0")])],"isStart":true});
            var sketch = newSketch(context, id + "F7", { "sketchPlane" : qUnion([Q0])});
            skLineSegment(sketch, "E7.bottom", {"start": v(13.3, -0.6) * mm, "end": v(54.34, -0.6) * mm});
            skLineSegment(sketch, "E7.top", {"start": v(13.3, 0.66) * mm, "end": v(54.34, 0.66) * mm});
            skLineSegment(sketch, "E7.left", {"start": v(54.34, -0.6) * mm, "end": v(54.34, 0.66) * mm});
            skLineSegment(sketch, "E7.right", {"start": v(13.3, -0.6) * mm, "end": v(13.3, 0.66) * mm});
            skSolve(sketch);
        }
        {
            var Q0;
            Q0 = qSketchRegion(id + "F7", true);
            extrude(context, id + "F8", {"entities" : qUnion([Q0]), "operationType" : NewBodyOperationType.REMOVE, "oppositeDirection" : true, "depth" : 25.4 * mm, "offsetDistance" : 25.4 * mm});
        }
    });
